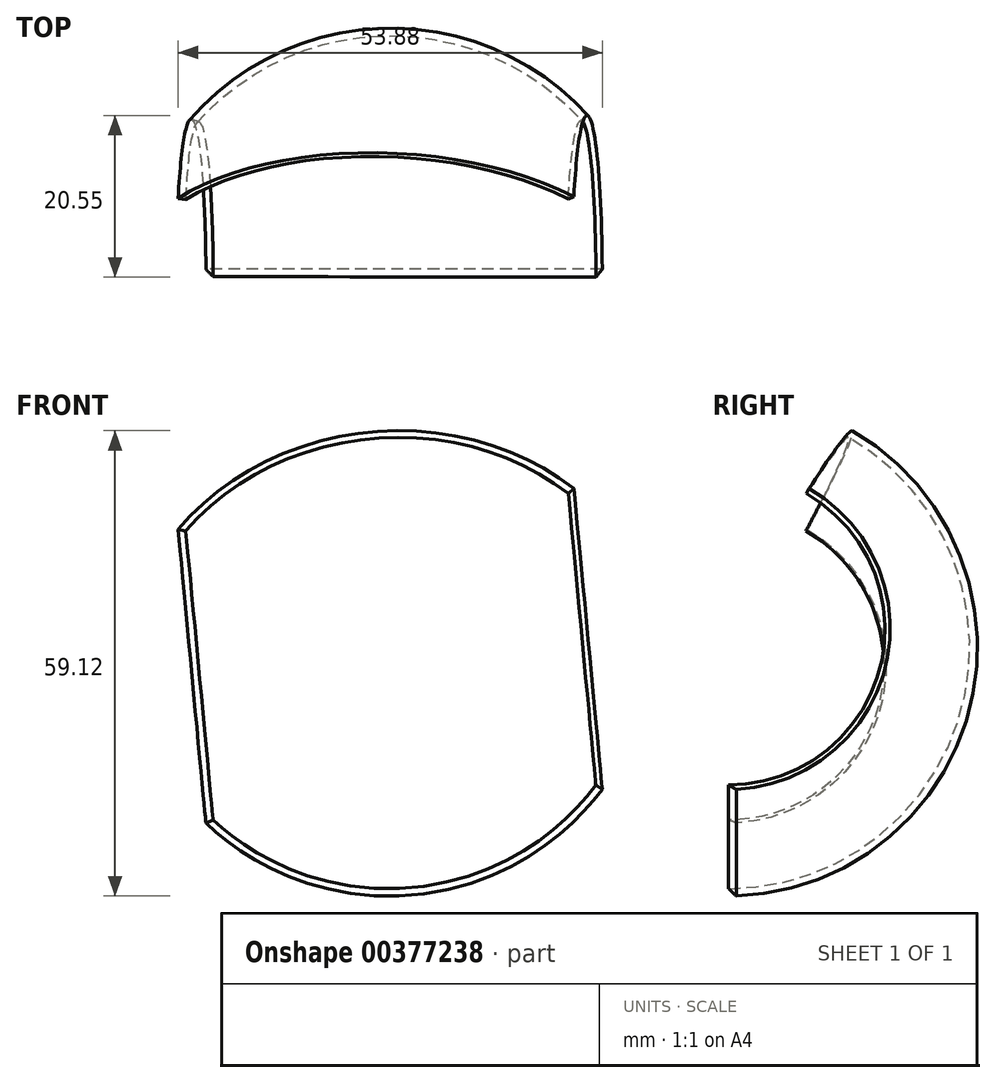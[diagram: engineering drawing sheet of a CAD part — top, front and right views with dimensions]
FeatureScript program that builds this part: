
annotation { "Feature Type Name" : "Feature", "Feature Type Description" : "" }
export const myFeature = defineFeature(function(context is Context, id is Id, definition is map)
    precondition{}
    {
        {
            var Q0;
            Q0=qCreatedBy(makeId("Front.planeOp"),FACE);
            var sketch = newSketch(context, id + "F0", { "sketchPlane" : qUnion([Q0])});
            skArc(sketch, "E0", {"start": v(-48.61, -4.45) * mm, "mid": v(-23.32, -13.02) * mm, "end": v(0, 0) * mm});
            skLineSegment(sketch, "E1", {"start": v(0, 0) * mm, "end": v(0.82, -0.57) * mm});
            skLineSegment(sketch, "E2", {"start": v(-48.61, -4.45) * mm, "end": v(-49.53, -4.84) * mm});
            skArc(sketch, "E3", {"start": v(-49.53, -4.84) * mm, "mid": v(-23.4, -14) * mm, "end": v(0.82, -0.57) * mm});
            skLineSegment(sketch, "E4", {"start": v(-48.27, 15.45) * mm, "end": v(-3.24, 19.71) * mm, "construction": true});
            skSolve(sketch);
        }
        {
            var Q0;
            Q0=makeQuery(id+"F0.imprint","IMPRINT",FACE,{"disambiguationData":[TD([[makeQuery(id+"F0.imprint","IMPRINT",EDGE,{"derivedFrom":sQuery(id+"F0.wireOp",EDGE,"E0")}),-1.0]])]});
            var Q1;
            Q1=sQuery(id+"F0.wireOp",EDGE,"E4");
            revolve(context, id + "F1", {"entities" : qUnion([Q0]), "axis" : qUnion([Q1]), "revolveType" : RevolveType.ONE_DIRECTION, "angle" : 150 * degree});
        }
        {
            var Q0;
            Q0=makeQuery(id+"F1.opRevolve","CAP_EDGE",EDGE,{"disambiguationData":[OSD([sQuery(id+"F0.wireOp",EDGE,"E3")])],"isStart":true});
            chamfer(context, id + "F2", {"entities" : qUnion([Q0]), "chamferType" : ChamferType.OFFSET_ANGLE, "width" : 1 * mm, "oppositeDirection" : false, "angle" : 45 * degree, "tangentPropagation" : true});
        }
    });
